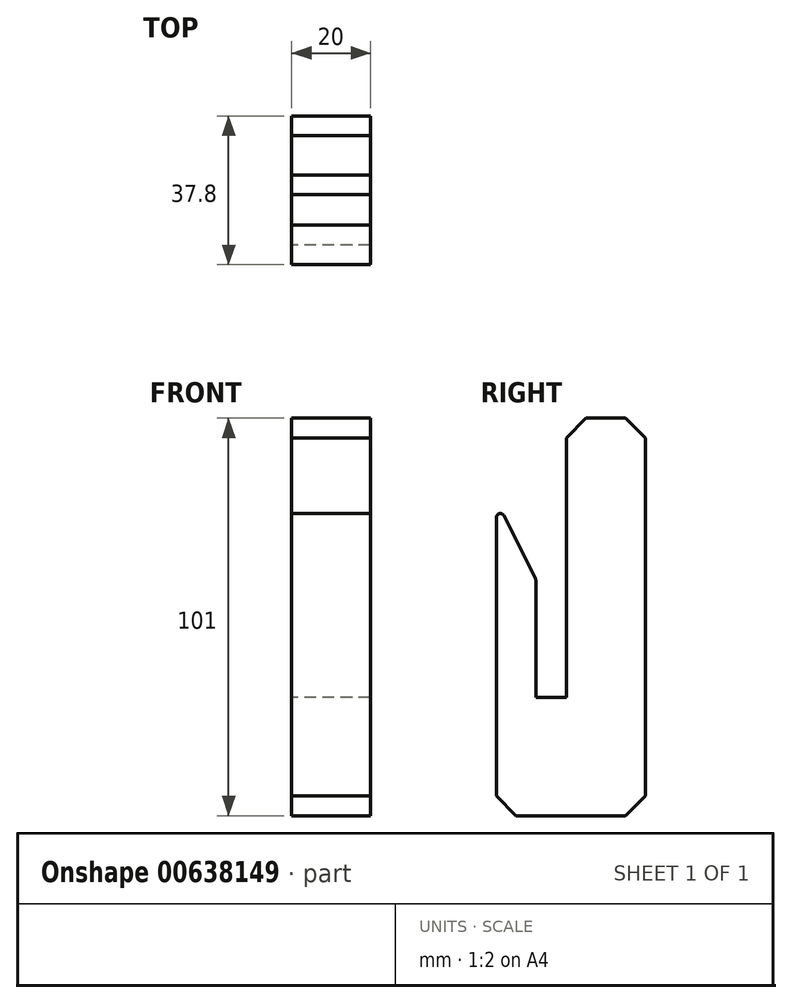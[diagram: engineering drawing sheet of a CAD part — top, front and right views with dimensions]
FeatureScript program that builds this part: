
annotation { "Feature Type Name" : "Feature", "Feature Type Description" : "" }
export const myFeature = defineFeature(function(context is Context, id is Id, definition is map)
    precondition{}
    {
        {
            var Q0;
            Q0=qCreatedBy(makeId("Front.planeOp"),FACE);
            var sketch = newSketch(context, id + "F0", { "sketchPlane" : qUnion([Q0])});
            skLineSegment(sketch, "E0.bottom", {"start": v(138.11, -109.5) * mm, "end": v(-138.11, -109.5) * mm, "construction": true});
            skLineSegment(sketch, "E0.top", {"start": v(138.11, 109.5) * mm, "end": v(-138.11, 109.5) * mm, "construction": true});
            skLineSegment(sketch, "E0.left", {"start": v(138.11, -109.5) * mm, "end": v(138.11, 109.5) * mm, "construction": true});
            skLineSegment(sketch, "E0.right", {"start": v(-138.11, -109.5) * mm, "end": v(-138.11, 109.5) * mm, "construction": true});
            skPoint(sketch, "E0.middle", {"position": v(0, 0) * mm});
            skSolve(sketch);
        }
        {
            var Q0;
            Q0=sQuery(id+"F0.wireOp",EDGE,"E0.right");
            cPlane(context, id + "F1", {"entities" : qUnion([Q0]), "cplaneType" : CPlaneType.LINE_ANGLE, "offset" : 25 * mm, "angle" : 0 * degree, "width" : 150 * mm, "height" : 150 * mm});
        }
        {
            var Q0;
            Q0=qCreatedBy(id+"F1.planeOp",FACE);
            var sketch = newSketch(context, id + "F2", { "sketchPlane" : qUnion([Q0])});
            skLineSegment(sketch, "E1", {"start": v(6.8, -39.5) * mm, "end": v(6.8, -110.5) * mm});
            skLineSegment(sketch, "E2", {"start": v(6.8, -110.5) * mm, "end": v(-1, -110.5) * mm});
            skLineSegment(sketch, "E3", {"start": v(-1, -110.5) * mm, "end": v(-1, -80.5) * mm});
            skLineSegment(sketch, "E4", {"start": v(-11, -60.5) * mm, "end": v(-11, -140.5) * mm});
            skLineSegment(sketch, "E5", {"start": v(-11, -140.5) * mm, "end": v(26.8, -140.5) * mm});
            skLineSegment(sketch, "E6", {"start": v(26.8, -140.5) * mm, "end": v(26.8, -39.5) * mm});
            skLineSegment(sketch, "E7", {"start": v(26.8, -39.5) * mm, "end": v(6.8, -39.5) * mm});
            skLineSegment(sketch, "E8", {"start": v(26.8, -59.5) * mm, "end": v(50.9, -59.5) * mm});
            skLineSegment(sketch, "E9", {"start": v(26.8, -120.5) * mm, "end": v(50.9, -120.5) * mm});
            skPoint(sketch, "E10.0", {"position": v(0, -109.5) * mm});
            skLineSegment(sketch, "E11", {"start": v(-1, -80.5) * mm, "end": v(-11, -60.5) * mm});
            skSolve(sketch);
        }
        {
            var Q0;
            Q0=makeQuery(id+"F2.imprint","IMPRINT",FACE,{"disambiguationData":[TD([[makeQuery(id+"F2.imprint","IMPRINT",EDGE,{"derivedFrom":sQuery(id+"F2.wireOp",EDGE,"E1")}),1.0]])]});
            extrude(context, id + "F3", {"entities" : qUnion([Q0]), "depth" : 20 * mm, "offsetDistance" : 25 * mm});
        }
        {
            var Q0;
            Q0=makeQuery(id+"F3.opExtrude","SWEPT_EDGE",EDGE,{"disambiguationData":[OSD([sQuery(id+"F2.wireOp",EDGE,"E6"),sQuery(id+"F2.wireOp",EDGE,"E7")])]});
            var Q1;
            Q1=makeQuery(id+"F3.opExtrude","SWEPT_EDGE",EDGE,{"disambiguationData":[OSD([sQuery(id+"F2.wireOp",EDGE,"E1"),sQuery(id+"F2.wireOp",EDGE,"E7")])]});
            var Q2;
            Q2=makeQuery(id+"F3.opExtrude","SWEPT_EDGE",EDGE,{"disambiguationData":[OSD([sQuery(id+"F2.wireOp",EDGE,"E4"),sQuery(id+"F2.wireOp",EDGE,"E5")])]});
            var Q3;
            Q3=makeQuery(id+"F3.opExtrude","SWEPT_EDGE",EDGE,{"disambiguationData":[OSD([sQuery(id+"F2.wireOp",EDGE,"E5"),sQuery(id+"F2.wireOp",EDGE,"E6")])]});
            chamfer(context, id + "F4", {"entities" : qUnion([Q0, Q1, Q2, Q3]), "width" : 5 * mm, "tangentPropagation" : true});
        }
        {
            var Q0;
            Q0=makeQuery(id+"F3.opExtrude","SWEPT_EDGE",EDGE,{"disambiguationData":[OSD([sQuery(id+"F2.wireOp",EDGE,"E4"),sQuery(id+"F2.wireOp",EDGE,"E11")])]});
            var Q1;
            Q1=makeQuery(id+"F3.opExtrude","SWEPT_EDGE",EDGE,{"disambiguationData":[OSD([sQuery(id+"F2.wireOp",EDGE,"E3"),sQuery(id+"F2.wireOp",EDGE,"E11")])]});
            fillet(context, id + "F5", {"entities" : qUnion([Q0, Q1]), "radius" : 1 * mm, "tangentPropagation" : true, "allowEdgeOverflow" : false});
        }
    });
